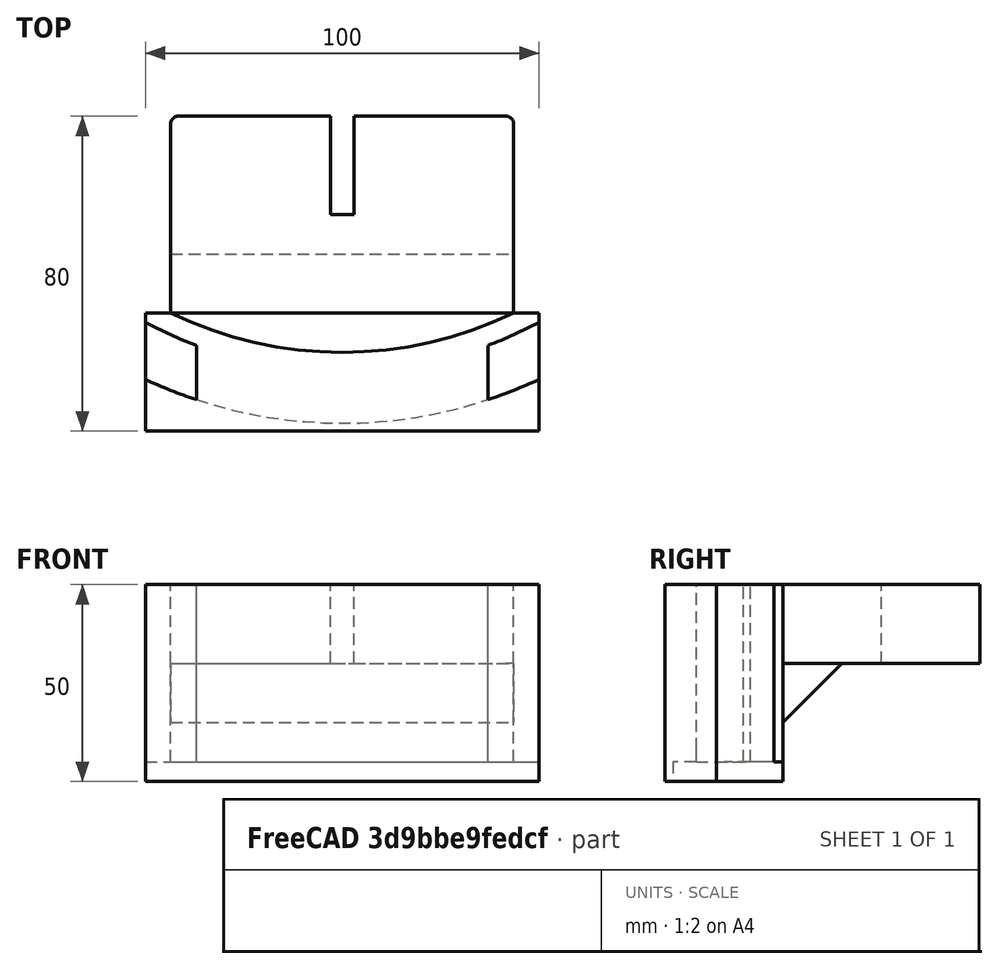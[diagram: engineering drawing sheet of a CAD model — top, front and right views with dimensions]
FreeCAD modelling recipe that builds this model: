
FCSTD DOCUMENT  (FreeCAD 0.19R24366 (Git))
Label: mgi_bag_clip
License: All rights reserved
LicenseURL: http://en.wikipedia.org/wiki/All_rights_reserved
objects: Part::FeaturePython×8, Part::Box×5, Part::Cut×4, Part::Cylinder×3, Part::Fuse×3, Part::Extrusion×3, App::DocumentObjectGroup×2, Part::Fillet×1, Part::Wedge×1, Part::MultiFuse×1
note: 29 computed .brp shape members not serialized (recipe doc carries the construction recipe); baked Part::Feature solids carry a one-line shape summary decoded from their .brp

FEATURE [Part::Box] Box  label="Cube"
  AttacherType = Attacher::AttachEngine3D
  Height = 5
  Length = 100
  Placement = pos=(-50,-120,0) rot=(0,0,1;0rad)
  Width = 30
FEATURE [Part::Cylinder] Cylinder
  Angle = 360
  AttacherType = Attacher::AttachEngine3D
  Height = 50
  Radius = 105
FEATURE [Part::Cylinder] Cylinder001
  Angle = 360
  AttacherType = Attacher::AttachEngine3D
  Height = 50
  Radius = 118
FEATURE [Part::Cut] Cut
  Base = -> Cylinder001
  Tool = -> Cylinder
FEATURE [Part::Box] Box001  label="Cube001"
  AttacherType = Attacher::AttachEngine3D
  Height = 50
  Length = 100
  Placement = pos=(-50,-120,0) rot=(0,0,1;0rad)
  Width = 30
FEATURE [Part::FeaturePython] Slice  # WARN: FeaturePython — macro-defined, semantics opaque (R4)
  Base = -> Cut
  Mode = 1
  Tolerance = 0
  Tools = -> [Box001]
FEATURE [App::DocumentObjectGroup] GrExplode_Slice  label="Exploded Slice"
FEATURE [Part::FeaturePython] Slice_child1  label="Slice.1"  # WARN: FeaturePython — macro-defined, semantics opaque (R4)
  Base = -> Slice
  FilterType = 1
  Invert = false
  OverrideMaxVal = 0
  WindowFrom = 80
  WindowTo = 100
  items = 1
FEATURE [Part::Box] Box002  label="Cube002"
  AttacherType = Attacher::AttachEngine3D
  Height = 50
  Length = 74
  Placement = pos=(-37,-120,5) rot=(0,0,1;0rad)
  Width = 30
FEATURE [Part::Cut] Cut001
  Base = -> Slice_child1
  Tool = -> Box002
FEATURE [Part::Fuse] Fusion
  Base = -> Box
  Tool = -> Cut001
FEATURE [Part::Cylinder] Cylinder002
  Angle = 360
  AttacherType = Attacher::AttachEngine3D
  Height = 50
  Radius = 100
FEATURE [Part::Box] Box003  label="Cube003"
  AttacherType = Attacher::AttachEngine3D
  Height = 50
  Length = 100
  Placement = pos=(-50,-120,0) rot=(0,0,1;0rad)
  Width = 30
FEATURE [Part::FeaturePython] Slice001  # WARN: FeaturePython — macro-defined, semantics opaque (R4)
  Base = -> Cylinder002
  Mode = 1
  Tolerance = 0
  Tools = -> [Box003]
FEATURE [Part::FeaturePython] Slice001_child1  label="Slice001.1"  # WARN: FeaturePython — macro-defined, semantics opaque (R4)
  Base = -> Slice001
  FilterType = 1
  Invert = false
  OverrideMaxVal = 0
  WindowFrom = 80
  WindowTo = 100
  items = 1
FEATURE [Part::Fuse] Fusion001
  Base = -> Fusion
  Tool = -> Slice001_child1
FEATURE [Part::FeaturePython] Facebinder  # WARN: FeaturePython — macro-defined, semantics opaque (R4)
  Area = 563.286
  Extrusion = 0
  Faces = -> [Fusion001]
  RemoveSplitter = false
  Sew = false
FEATURE [Part::Extrusion] Extrude
  Base = -> Facebinder
  Dir = (0,0,1)
  DirMode = 2
  FaceMakerClass = Part::FaceMakerBullseye
  LengthFwd = 10
  LengthRev = 0
  Placement = pos=(0,0,-7) rot=(0,0,1;0rad)
  Solid = true
  Symmetric = false
FEATURE [Part::Cut] Cut002
  Base = -> Fusion001
  Tool = -> Extrude
FEATURE [Part::FeaturePython] Facebinder001  # WARN: FeaturePython — macro-defined, semantics opaque (R4)
  Area = 3923.01
  Extrusion = 0
  Faces = -> [Cut002]
  RemoveSplitter = false
  Sew = false
FEATURE [Part::FeaturePython] Facebinder002  # WARN: FeaturePython — macro-defined, semantics opaque (R4)
  Area = 435.89
  Extrusion = 0
  Faces = -> [Cut002]
  RemoveSplitter = false
  Sew = false
FEATURE [Part::Extrusion] Extrude001
  Base = -> Facebinder001
  Dir = (0,1,0)
  DirMode = 2
  FaceMakerClass = Part::FaceMakerBullseye
  LengthFwd = 50
  LengthRev = 0
  Solid = false
  Symmetric = false
FEATURE [Part::FeaturePython] Facebinder003  # WARN: FeaturePython — macro-defined, semantics opaque (R4)
  Area = 4358.9
  Extrusion = 0
  Faces = -> [Extrude001]
  RemoveSplitter = false
  Sew = false
FEATURE [Part::Extrusion] Extrude002
  Base = -> Facebinder003
  Dir = (0,0,1)
  DirMode = 2
  FaceMakerClass = Part::FaceMakerBullseye
  LengthFwd = 20
  LengthRev = 0
  Reversed = true
  Solid = false
  Symmetric = false
FEATURE [Part::Box] Box004  label="Cube004"
  AttacherType = Attacher::AttachEngine3D
  Height = 50
  Length = 6
  Placement = pos=(-3,-65,5) rot=(0,0,1;0rad)
  Width = 32
FEATURE [Part::Cut] Cut003
  Base = -> Extrude002
  Tool = -> Box004
FEATURE [Part::Fuse] Fusion002
  Base = -> Cut002
  Tool = -> Cut003
FEATURE [App::DocumentObjectGroup] GrExplode_Slice001  label="Exploded Slice001"
  Group = -> [Fusion002]
FEATURE [Part::Fillet] Fillet
  Base = -> Fusion002
  Edges = 2 edges r=2: [Edge10,Edge20]
FEATURE [Part::Wedge] Wedge
  AttacherType = Attacher::AttachEngine3D
  Placement = pos=(-43.59,-90,30) rot=(-1,0,0;1.5708rad)
  X2max = 87.18
  X2min = 0
  Xmax = 87.18
  Xmin = 0
  Ymax = 15
  Ymin = 0
  Z2max = 0
  Z2min = 0
  Zmax = 15
  Zmin = 0
FEATURE [Part::MultiFuse] Fusion003
  Shapes = -> [Fillet,Wedge]
